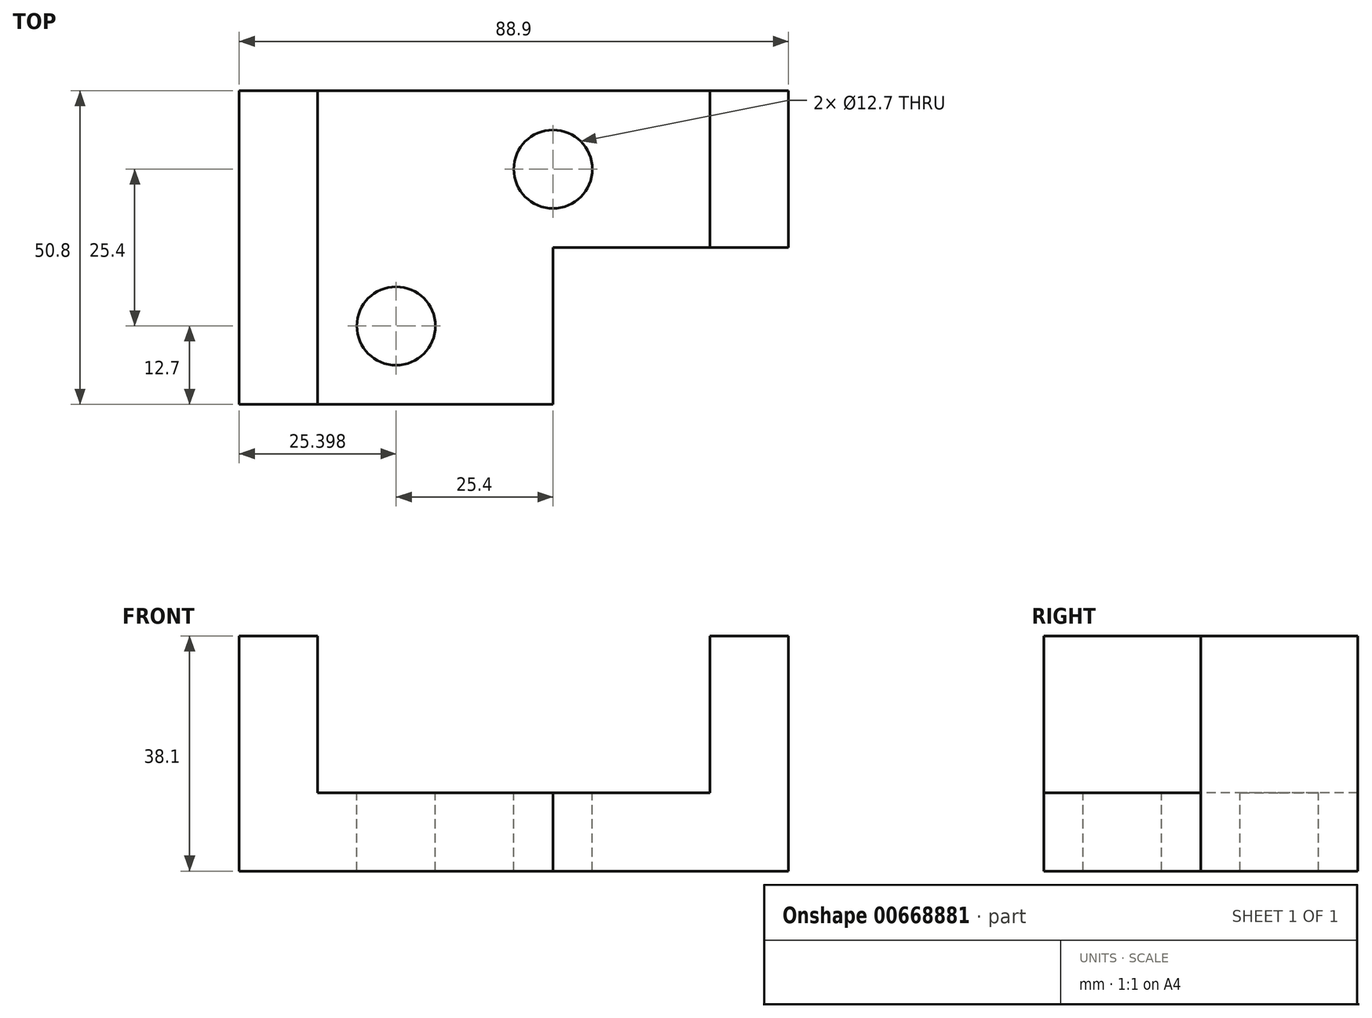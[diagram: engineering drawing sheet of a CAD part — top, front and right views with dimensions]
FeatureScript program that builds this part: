
annotation { "Feature Type Name" : "Feature", "Feature Type Description" : "" }
export const myFeature = defineFeature(function(context is Context, id is Id, definition is map)
    precondition{}
    {
        {
            var Q0;
            Q0=qCreatedBy(makeId("Front.planeOp"),FACE);
            var sketch = newSketch(context, id + "F0", { "sketchPlane" : qUnion([Q0])});
            skLineSegment(sketch, "E0.bottom", {"start": v(-5.93, 24.13) * mm, "end": v(-94.83, 24.13) * mm});
            skLineSegment(sketch, "E0.top", {"start": v(-5.93, 62.23) * mm, "end": v(-94.83, 62.23) * mm});
            skLineSegment(sketch, "E0.left", {"start": v(-5.93, 24.13) * mm, "end": v(-5.93, 62.23) * mm});
            skLineSegment(sketch, "E0.right", {"start": v(-94.83, 24.13) * mm, "end": v(-94.83, 62.23) * mm});
            skPoint(sketch, "E0.middle", {"position": v(-50.38, 43.18) * mm});
            skSolve(sketch);
        }
        {
            var Q0;
            Q0=makeQuery(id+"F0.imprint","IMPRINT",FACE,{"disambiguationData":[TD([[makeQuery(id+"F0.imprint","IMPRINT",EDGE,{"derivedFrom":sQuery(id+"F0.wireOp",EDGE,"E0.bottom")}),-1.0]])]});
            extrude(context, id + "F1", {"entities" : qUnion([Q0]), "depth" : 50.8 * mm, "offsetDistance" : 25.4 * mm});
        }
        {
            var Q0;
            Q0=makeQuery(id+"F1.opExtrude","CAP_FACE",FACE,{"disambiguationData":[OSD([sQuery(id+"F0.wireOp",EDGE,"E0.bottom"),sQuery(id+"F0.wireOp",EDGE,"E0.top"),sQuery(id+"F0.wireOp",EDGE,"E0.left"),sQuery(id+"F0.wireOp",EDGE,"E0.right")])],"isStart":false});
            var sketch = newSketch(context, id + "F2", { "sketchPlane" : qUnion([Q0])});
            skLineSegment(sketch, "E1.bottom", {"start": v(-82.13, 62.23) * mm, "end": v(-18.63, 62.23) * mm});
            skLineSegment(sketch, "E1.top", {"start": v(-82.13, 36.83) * mm, "end": v(-18.63, 36.83) * mm});
            skLineSegment(sketch, "E1.left", {"start": v(-82.13, 62.23) * mm, "end": v(-82.13, 36.83) * mm});
            skLineSegment(sketch, "E1.right", {"start": v(-18.63, 62.23) * mm, "end": v(-18.63, 36.83) * mm});
            skSolve(sketch);
        }
        {
            var Q0;
            Q0 = qSketchRegion(id + "F2", true);
            extrude(context, id + "F3", {"entities" : qUnion([Q0]), "operationType" : NewBodyOperationType.REMOVE, "endBound" : BoundingType.THROUGH_ALL, "oppositeDirection" : true, "depth" : 25.4 * mm, "offsetDistance" : 25.4 * mm});
        }
        {
            var Q0;
            {var subQ1=sQuery(id+"F0.wireOp",EDGE,"E0.left");var subQ2=sQuery(id+"F0.wireOp",EDGE,"E0.top");Q0=makeQuery(id+"F3.boolean.opBoolean","SPLIT",FACE,{"disambiguationData":[TD([makeQuery(id+"F1.opExtrude","SWEPT_FACE",FACE,{"disambiguationData":[OSD([subQ1])]})])],"derivedFrom":makeQuery(id+"F1.opExtrude","SWEPT_FACE",FACE,{"disambiguationData":[OSD([subQ2])]})});}
            var sketch = newSketch(context, id + "F4", { "sketchPlane" : qUnion([Q0])});
            skLineSegment(sketch, "E2.bottom", {"start": v(-5.93, -50.8) * mm, "end": v(-44.03, -50.8) * mm});
            skLineSegment(sketch, "E2.top", {"start": v(-5.93, -25.4) * mm, "end": v(-44.03, -25.4) * mm});
            skLineSegment(sketch, "E2.left", {"start": v(-5.93, -50.8) * mm, "end": v(-5.93, -25.4) * mm});
            skLineSegment(sketch, "E2.right", {"start": v(-44.03, -50.8) * mm, "end": v(-44.03, -25.4) * mm});
            skSolve(sketch);
        }
        {
            var Q0;
            Q0 = qSketchRegion(id + "F4", true);
            extrude(context, id + "F5", {"entities" : qUnion([Q0]), "operationType" : NewBodyOperationType.REMOVE, "endBound" : BoundingType.THROUGH_ALL, "oppositeDirection" : true, "depth" : 25.4 * mm, "offsetDistance" : 25.4 * mm});
        }
        {
            var Q0;
            Q0=makeQuery(id+"F3.boolean.opBoolean","COPY",FACE,{"derivedFrom":makeQuery(id+"F3.opExtrude","SWEPT_FACE",FACE,{"disambiguationData":[OSD([sQuery(id+"F2.wireOp",EDGE,"E1.top")])]})});
            var sketch = newSketch(context, id + "F6", { "sketchPlane" : qUnion([Q0])});
            skCircle(sketch, "E3", {"center": v(-44.03, -12.7) * mm, "radius": 6.35 * mm});
            skSolve(sketch);
        }
        {
            var Q0;
            Q0=makeQuery(id+"F6.imprint","IMPRINT",FACE,{"disambiguationData":[TD([[makeQuery(id+"F6.imprint","IMPRINT",EDGE,{"derivedFrom":sQuery(id+"F6.wireOp",EDGE,"E3")}),1.0]])]});
            extrude(context, id + "F7", {"entities" : qUnion([Q0]), "operationType" : NewBodyOperationType.REMOVE, "endBound" : BoundingType.THROUGH_ALL, "oppositeDirection" : true, "depth" : 25.4 * mm, "offsetDistance" : 25.4 * mm});
        }
        {
            var Q0;
            Q0=makeQuery(id+"F3.boolean.opBoolean","COPY",FACE,{"derivedFrom":makeQuery(id+"F3.opExtrude","SWEPT_FACE",FACE,{"disambiguationData":[OSD([sQuery(id+"F2.wireOp",EDGE,"E1.top")])]})});
            var sketch = newSketch(context, id + "F8", { "sketchPlane" : qUnion([Q0])});
            skCircle(sketch, "E4", {"center": v(-69.43, -38.1) * mm, "radius": 6.35 * mm});
            skSolve(sketch);
        }
        {
            var Q0;
            Q0=makeQuery(id+"F8.imprint","IMPRINT",FACE,{"disambiguationData":[TD([[makeQuery(id+"F8.imprint","IMPRINT",EDGE,{"derivedFrom":sQuery(id+"F8.wireOp",EDGE,"E4")}),1.0]])]});
            extrude(context, id + "F9", {"entities" : qUnion([Q0]), "operationType" : NewBodyOperationType.REMOVE, "endBound" : BoundingType.THROUGH_ALL, "oppositeDirection" : true, "depth" : 25.4 * mm, "offsetDistance" : 25.4 * mm});
        }
    });
